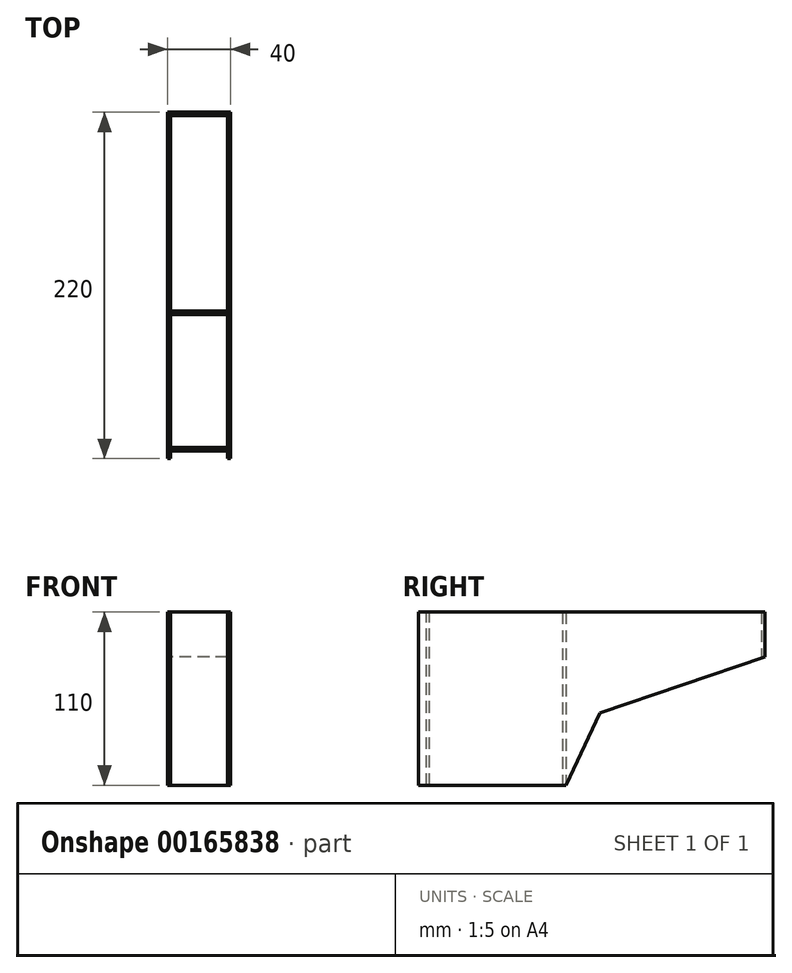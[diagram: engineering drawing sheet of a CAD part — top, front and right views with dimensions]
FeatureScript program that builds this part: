
annotation { "Feature Type Name" : "Feature", "Feature Type Description" : "" }
export const myFeature = defineFeature(function(context is Context, id is Id, definition is map)
    precondition{}
    {
        {
            var Q0;
            Q0=qCreatedBy(makeId("Right.planeOp"),FACE);
            var sketch = newSketch(context, id + "F0", { "sketchPlane" : qUnion([Q0])});
            skLineSegment(sketch, "E0", {"start": v(-143.47, 0) * mm, "end": v(-143.47, -110) * mm});
            skLineSegment(sketch, "E1", {"start": v(-143.47, -110) * mm, "end": v(-49.82, -110) * mm});
            skLineSegment(sketch, "E2", {"start": v(-49.82, -110) * mm, "end": v(-28.17, -64.06) * mm});
            skLineSegment(sketch, "E3", {"start": v(-28.17, -64.06) * mm, "end": v(76.53, -28.5) * mm});
            skLineSegment(sketch, "E4", {"start": v(76.53, -28.5) * mm, "end": v(76.53, 0) * mm});
            skLineSegment(sketch, "E5", {"start": v(76.53, 0) * mm, "end": v(-143.47, 0) * mm});
            skSolve(sketch);
        }
        {
            var Q0;
            Q0 = qSketchRegion(id + "F0", true);
            extrude(context, id + "F1", {"entities" : qUnion([Q0]), "endBound" : BoundingType.SYMMETRIC, "depth" : 40 * mm});
        }
        {
            var Q0;
            Q0=makeQuery(id+"F1.opExtrude","SWEPT_FACE",FACE,{"disambiguationData":[OSD([sQuery(id+"F0.wireOp",EDGE,"E5")])]});
            var sketch = newSketch(context, id + "F2", { "sketchPlane" : qUnion([Q0])});
            skLineSegment(sketch, "E6.bottom", {"start": v(-18, 76.53) * mm, "end": v(18, 76.53) * mm});
            skLineSegment(sketch, "E6.top", {"start": v(-18, -143.47) * mm, "end": v(18, -143.47) * mm});
            skLineSegment(sketch, "E6.left", {"start": v(-18, 76.53) * mm, "end": v(-18, -143.47) * mm});
            skLineSegment(sketch, "E6.right", {"start": v(18, 76.53) * mm, "end": v(18, -143.47) * mm});
            skSolve(sketch);
        }
        {
            var Q0;
            Q0 = qSketchRegion(id + "F2", true);
            extrude(context, id + "F3", {"entities" : qUnion([Q0]), "operationType" : NewBodyOperationType.REMOVE, "oppositeDirection" : true, "depth" : 157 * mm});
        }
        {
            var Q0;
            Q0=makeQuery(id+"F3.boolean.opBoolean","COPY",FACE,{"derivedFrom":makeQuery(id+"F3.opExtrude","SWEPT_FACE",FACE,{"disambiguationData":[OSD([sQuery(id+"F2.wireOp",EDGE,"E6.left")])]})});
            var sketch = newSketch(context, id + "F4", { "sketchPlane" : qUnion([Q0])});
            skLineSegment(sketch, "E7.bottom", {"start": v(-136.47, 0) * mm, "end": v(-138.47, 0) * mm});
            skLineSegment(sketch, "E7.top", {"start": v(-136.47, -110) * mm, "end": v(-138.47, -110) * mm});
            skLineSegment(sketch, "E7.left", {"start": v(-136.47, 0) * mm, "end": v(-136.47, -110) * mm});
            skLineSegment(sketch, "E7.right", {"start": v(-138.47, 0) * mm, "end": v(-138.47, -110) * mm});
            skLineSegment(sketch, "E8.bottom", {"start": v(-49.82, -110) * mm, "end": v(-51.82, -110) * mm});
            skLineSegment(sketch, "E8.top", {"start": v(-49.82, 0) * mm, "end": v(-51.82, 0) * mm});
            skLineSegment(sketch, "E8.left", {"start": v(-49.82, -110) * mm, "end": v(-49.82, 0) * mm});
            skLineSegment(sketch, "E8.right", {"start": v(-51.82, -110) * mm, "end": v(-51.82, 0) * mm});
            skLineSegment(sketch, "E9.bottom", {"start": v(76.53, -28.5) * mm, "end": v(74.53, -28.5) * mm});
            skLineSegment(sketch, "E9.top", {"start": v(76.53, 0) * mm, "end": v(74.53, 0) * mm});
            skLineSegment(sketch, "E9.left", {"start": v(76.53, -28.5) * mm, "end": v(76.53, 0) * mm});
            skLineSegment(sketch, "E9.right", {"start": v(74.53, -28.5) * mm, "end": v(74.53, 0) * mm});
            skSolve(sketch);
        }
        {
            var Q0;
            Q0=makeQuery(id+"F4.imprint","IMPRINT",FACE,{"disambiguationData":[TD([[makeQuery(id+"F4.imprint","IMPRINT",EDGE,{"derivedFrom":sQuery(id+"F4.wireOp",EDGE,"E7.bottom")}),1.0]])]});
            var Q1;
            Q1=makeQuery(id+"F4.imprint","IMPRINT",FACE,{"disambiguationData":[TD([[makeQuery(id+"F4.imprint","IMPRINT",EDGE,{"derivedFrom":sQuery(id+"F4.wireOp",EDGE,"E8.bottom")}),-1.0]])]});
            var Q2;
            Q2=makeQuery(id+"F4.imprint","IMPRINT",FACE,{"disambiguationData":[TD([[makeQuery(id+"F4.imprint","IMPRINT",EDGE,{"derivedFrom":sQuery(id+"F4.wireOp",EDGE,"E9.bottom")}),-1.0]])]});
            var Q3;
            Q3=makeQuery(id+"F3.boolean.opBoolean","COPY",FACE,{"derivedFrom":makeQuery(id+"F3.opExtrude","SWEPT_FACE",FACE,{"disambiguationData":[OSD([sQuery(id+"F2.wireOp",EDGE,"E6.right")])]})});
            extrude(context, id + "F5", {"entities" : qUnion([Q0, Q1, Q2]), "endBound" : BoundingType.UP_TO_SURFACE, "endBoundEntityFace" : qUnion([Q3]), "depth" : 25 * mm});
        }
    });
